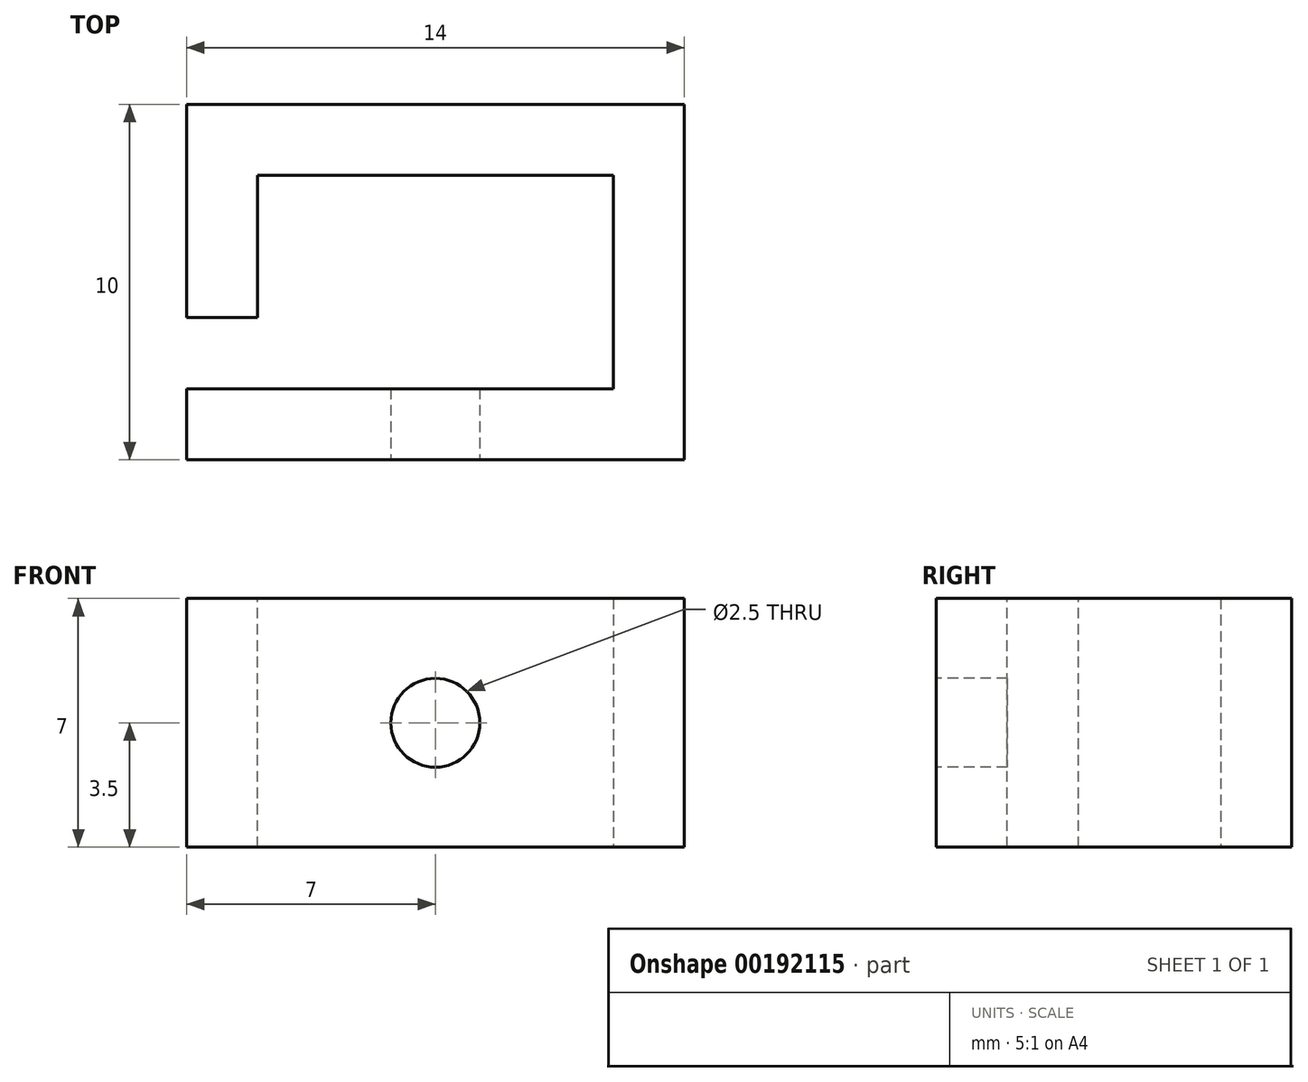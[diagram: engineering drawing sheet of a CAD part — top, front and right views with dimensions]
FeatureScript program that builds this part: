
annotation { "Feature Type Name" : "Feature", "Feature Type Description" : "" }
export const myFeature = defineFeature(function(context is Context, id is Id, definition is map)
    precondition{}
    {
        {
            var Q0;
            Q0=qCreatedBy(makeId("Top.planeOp"),FACE);
            var sketch = newSketch(context, id + "F0", { "sketchPlane" : qUnion([Q0])});
            skLineSegment(sketch, "E0.bottom", {"start": v(-7, 5) * mm, "end": v(7, 5) * mm});
            skLineSegment(sketch, "E0.top", {"start": v(-7, -5) * mm, "end": v(7, -5) * mm});
            skLineSegment(sketch, "E0.left", {"start": v(-7, 5) * mm, "end": v(-7, -5) * mm});
            skLineSegment(sketch, "E0.right", {"start": v(7, 5) * mm, "end": v(7, -5) * mm});
            skLineSegment(sketch, "E1.bottom", {"start": v(-5, 3) * mm, "end": v(5, 3) * mm});
            skLineSegment(sketch, "E1.top", {"start": v(-5, -3) * mm, "end": v(5, -3) * mm});
            skLineSegment(sketch, "E1.left", {"start": v(-5, 3) * mm, "end": v(-5, -3) * mm});
            skLineSegment(sketch, "E1.right", {"start": v(5, 3) * mm, "end": v(5, -3) * mm});
            skSolve(sketch);
        }
        {
            var Q0;
            Q0=makeQuery(id+"F0.imprint","IMPRINT",FACE,{"disambiguationData":[TD([[makeQuery(id+"F0.imprint","IMPRINT",EDGE,{"derivedFrom":sQuery(id+"F0.wireOp",EDGE,"E0.bottom")}),-1.0]])]});
            extrude(context, id + "F1", {"entities" : qUnion([Q0]), "depth" : 7 * mm});
        }
        {
            var Q0;
            Q0=makeQuery(id+"F1.opExtrude","CAP_FACE",FACE,{"disambiguationData":[OSD([sQuery(id+"F0.wireOp",EDGE,"E0.bottom"),sQuery(id+"F0.wireOp",EDGE,"E0.top"),sQuery(id+"F0.wireOp",EDGE,"E0.left"),sQuery(id+"F0.wireOp",EDGE,"E0.right"),sQuery(id+"F0.wireOp",EDGE,"E1.bottom"),sQuery(id+"F0.wireOp",EDGE,"E1.top"),sQuery(id+"F0.wireOp",EDGE,"E1.left"),sQuery(id+"F0.wireOp",EDGE,"E1.right")])],"isStart":false});
            var sketch = newSketch(context, id + "F2", { "sketchPlane" : qUnion([Q0])});
            skLineSegment(sketch, "E2.bottom", {"start": v(-9.72, -1) * mm, "end": v(-3.76, -1) * mm});
            skLineSegment(sketch, "E2.top", {"start": v(-9.72, -3) * mm, "end": v(-3.76, -3) * mm});
            skLineSegment(sketch, "E2.left", {"start": v(-9.72, -1) * mm, "end": v(-9.72, -3) * mm});
            skLineSegment(sketch, "E2.right", {"start": v(-3.76, -1) * mm, "end": v(-3.76, -3) * mm});
            skSolve(sketch);
        }
        {
            var Q0;
            {var subQ0=sQuery(id+"F2.wireOp",EDGE,"E2.bottom");var subQ1=makeQuery(id+"F1.opExtrude","CAP_EDGE",EDGE,{"disambiguationData":[OSD([sQuery(id+"F0.wireOp",EDGE,"E0.left")])],"isStart":false});var subQ2=makeQuery(id+"F2.imprint","INTERSECT",VERTEX,{"derivedFrom":[subQ1,subQ0]});Q0=makeQuery(id+"F2.imprint","IMPRINT",FACE,{"disambiguationData":[TD([[makeQuery(id+"F2.imprint","IMPRINT",EDGE,{"disambiguationData":[TD([[subQ2,-1.0]])],"derivedFrom":subQ0}),-1.0]])]});}
            extrude(context, id + "F3", {"entities" : qUnion([Q0]), "operationType" : NewBodyOperationType.REMOVE, "oppositeDirection" : true, "depth" : 10 * mm});
        }
        {
            var Q0;
            Q0=makeQuery(id+"F1.opExtrude","SWEPT_FACE",FACE,{"disambiguationData":[OSD([sQuery(id+"F0.wireOp",EDGE,"E0.top")])]});
            var sketch = newSketch(context, id + "F4", { "sketchPlane" : qUnion([Q0])});
            skCircle(sketch, "E3", {"center": v(0, 3.5) * mm, "radius": 1.25 * mm});
            skSolve(sketch);
        }
        {
            var Q0;
            Q0=makeQuery(id+"F4.imprint","IMPRINT",FACE,{"disambiguationData":[TD([[makeQuery(id+"F4.imprint","IMPRINT",EDGE,{"derivedFrom":sQuery(id+"F4.wireOp",EDGE,"E3")}),1.0]])]});
            extrude(context, id + "F5", {"entities" : qUnion([Q0]), "operationType" : NewBodyOperationType.REMOVE, "oppositeDirection" : true, "depth" : 5 * mm});
        }
    });
